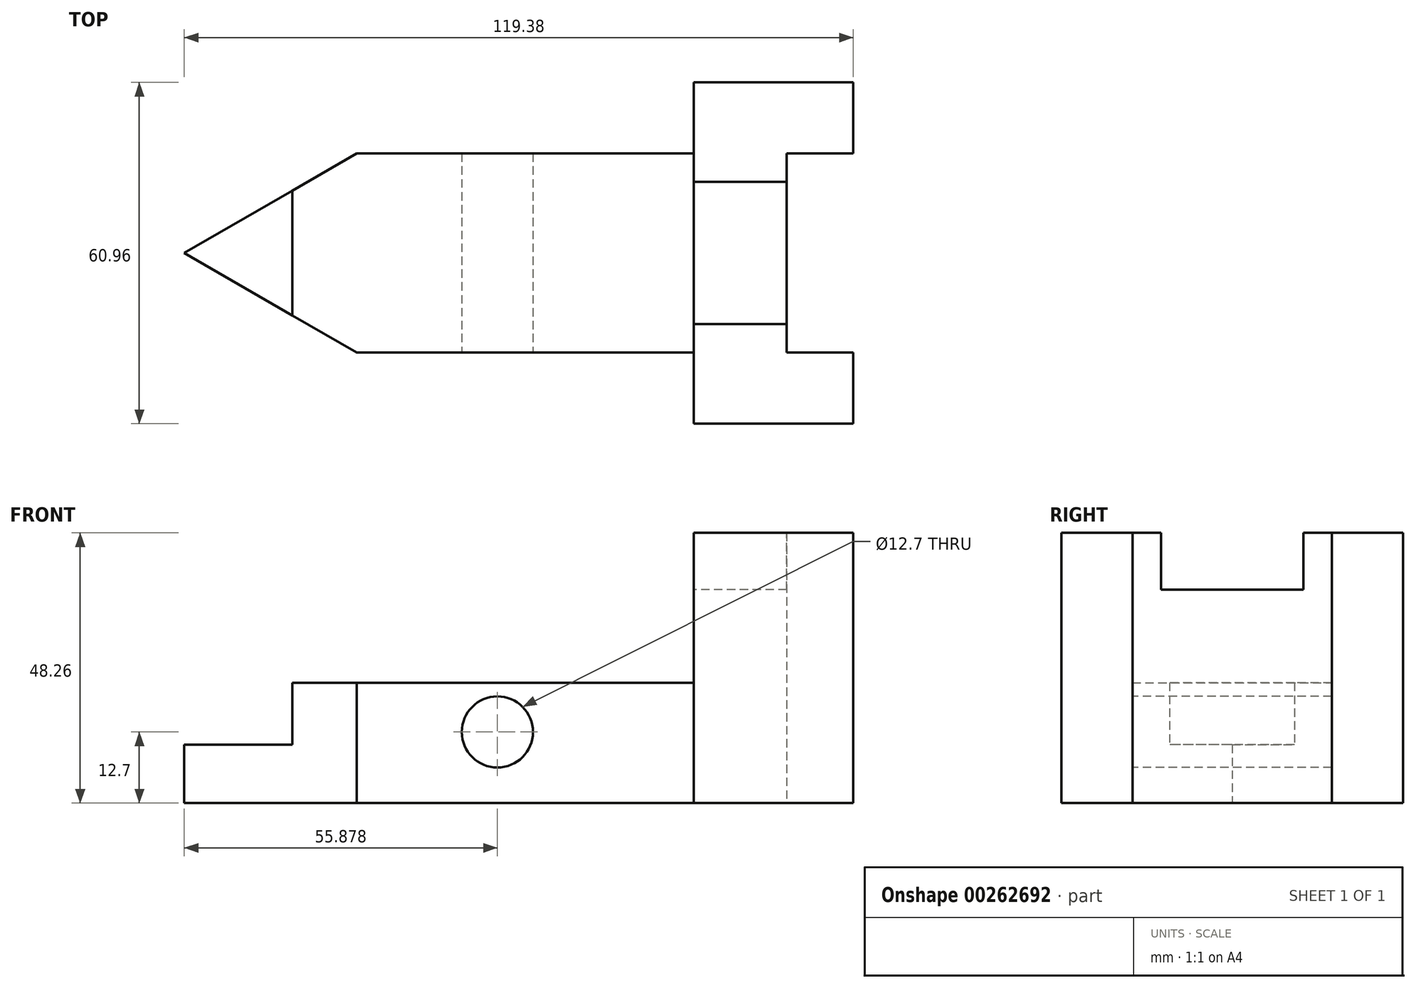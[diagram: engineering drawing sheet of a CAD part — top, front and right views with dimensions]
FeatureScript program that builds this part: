
annotation { "Feature Type Name" : "Feature", "Feature Type Description" : "" }
export const myFeature = defineFeature(function(context is Context, id is Id, definition is map)
    precondition{}
    {
        {
            var Q0;
            Q0=qCreatedBy(makeId("Top.planeOp"),FACE);
            var sketch = newSketch(context, id + "F0", { "sketchPlane" : qUnion([Q0])});
            skLineSegment(sketch, "E0.bottom", {"start": v(59.83, 28.5) * mm, "end": v(31.38, 28.5) * mm});
            skLineSegment(sketch, "E0.top", {"start": v(59.83, -32.46) * mm, "end": v(31.38, -32.46) * mm});
            skLineSegment(sketch, "E0.left", {"start": v(59.83, 28.5) * mm, "end": v(59.83, -32.46) * mm});
            skLineSegment(sketch, "E1", {"start": v(31.38, 28.5) * mm, "end": v(31.38, 15.8) * mm});
            skLineSegment(sketch, "E2.bottom", {"start": v(31.38, 15.8) * mm, "end": v(-28.76, 15.8) * mm});
            skLineSegment(sketch, "E2.top", {"start": v(31.38, -19.76) * mm, "end": v(-28.76, -19.76) * mm});
            skLineSegment(sketch, "E3", {"start": v(-59.55, -1.98) * mm, "end": v(-28.76, 15.8) * mm});
            skLineSegment(sketch, "E4", {"start": v(-59.55, -1.98) * mm, "end": v(-28.76, -19.76) * mm});
            skLineSegment(sketch, "E5.trimOffspring", {"start": v(31.38, -19.76) * mm, "end": v(31.38, -32.46) * mm});
            skSolve(sketch);
        }
        {
            var Q0;
            Q0 = qSketchRegion(id + "F0", true);
            extrude(context, id + "F1", {"entities" : qUnion([Q0]), "depth" : 48.26 * mm});
        }
        {
            var Q0;
            Q0=qCreatedBy(makeId("Front.planeOp"),FACE);
            var sketch = newSketch(context, id + "F2", { "sketchPlane" : qUnion([Q0])});
            skCircle(sketch, "E6", {"center": v(-3.67, 12.7) * mm, "radius": 6.35 * mm});
            skSolve(sketch);
        }
        {
            var Q0;
            Q0 = qSketchRegion(id + "F2", true);
            extrude(context, id + "F3", {"entities" : qUnion([Q0]), "operationType" : NewBodyOperationType.REMOVE, "endBound" : BoundingType.SYMMETRIC, "oppositeDirection" : true, "depth" : 40.13 * mm});
        }
        {
            var Q0;
            Q0=qCreatedBy(makeId("Front.planeOp"),FACE);
            var sketch = newSketch(context, id + "F4", { "sketchPlane" : qUnion([Q0])});
            skLineSegment(sketch, "E7.bottom", {"start": v(31.38, 48.3) * mm, "end": v(-59.55, 48.3) * mm});
            skLineSegment(sketch, "E7.top", {"start": v(31.38, 21.5) * mm, "end": v(-59.55, 21.5) * mm});
            skLineSegment(sketch, "E7.left", {"start": v(31.38, 48.3) * mm, "end": v(31.38, 21.5) * mm});
            skLineSegment(sketch, "E7.right", {"start": v(-59.55, 48.3) * mm, "end": v(-59.55, 21.5) * mm});
            skSolve(sketch);
        }
        {
            var Q0;
            Q0 = qSketchRegion(id + "F4", true);
            extrude(context, id + "F5", {"entities" : qUnion([Q0]), "operationType" : NewBodyOperationType.REMOVE, "endBound" : BoundingType.SYMMETRIC, "depth" : 127 * mm});
        }
        {
            var Q0;
            Q0=qCreatedBy(makeId("Top.planeOp"),FACE);
            var sketch = newSketch(context, id + "F6", { "sketchPlane" : qUnion([Q0])});
            skLineSegment(sketch, "E8.bottom", {"start": v(60.11, 15.8) * mm, "end": v(47.97, 15.8) * mm});
            skLineSegment(sketch, "E8.top", {"start": v(60.11, -19.76) * mm, "end": v(47.97, -19.76) * mm});
            skLineSegment(sketch, "E8.left", {"start": v(60.11, 15.8) * mm, "end": v(60.11, -19.76) * mm});
            skLineSegment(sketch, "E8.right", {"start": v(47.97, 15.8) * mm, "end": v(47.97, -19.76) * mm});
            skSolve(sketch);
        }
        {
            var Q0;
            Q0 = qSketchRegion(id + "F6", true);
            extrude(context, id + "F7", {"entities" : qUnion([Q0]), "operationType" : NewBodyOperationType.REMOVE, "depth" : 70.87 * mm});
        }
        {
            var Q0;
            Q0=makeQuery(id+"F1.opExtrude","CAP_FACE",FACE,{"disambiguationData":[OSD([sQuery(id+"F0.wireOp",EDGE,"E0.bottom"),sQuery(id+"F0.wireOp",EDGE,"E0.top"),sQuery(id+"F0.wireOp",EDGE,"E0.left"),sQuery(id+"F0.wireOp",EDGE,"E1"),sQuery(id+"F0.wireOp",EDGE,"E2.bottom"),sQuery(id+"F0.wireOp",EDGE,"E2.top"),sQuery(id+"F0.wireOp",EDGE,"E3"),sQuery(id+"F0.wireOp",EDGE,"E4"),sQuery(id+"F0.wireOp",EDGE,"E5.trimOffspring")])],"isStart":false});
            var sketch = newSketch(context, id + "F8", { "sketchPlane" : qUnion([Q0])});
            skLineSegment(sketch, "E9.bottom", {"start": v(56.8, 10.72) * mm, "end": v(21.02, 10.72) * mm});
            skLineSegment(sketch, "E9.top", {"start": v(56.8, -14.68) * mm, "end": v(21.02, -14.68) * mm});
            skLineSegment(sketch, "E9.left", {"start": v(56.8, 10.72) * mm, "end": v(56.8, -14.68) * mm});
            skLineSegment(sketch, "E9.right", {"start": v(21.02, 10.72) * mm, "end": v(21.02, -14.68) * mm});
            skSolve(sketch);
        }
        {
            var Q0;
            Q0 = qSketchRegion(id + "F8", true);
            extrude(context, id + "F9", {"entities" : qUnion([Q0]), "operationType" : NewBodyOperationType.REMOVE, "oppositeDirection" : true, "depth" : 10.16 * mm});
        }
        {
            var Q0;
            Q0=qCreatedBy(makeId("Top.planeOp"),FACE);
            var sketch = newSketch(context, id + "F10", { "sketchPlane" : qUnion([Q0])});
            skLineSegment(sketch, "E10.bottom", {"start": v(-40.25, 20.23) * mm, "end": v(-59.55, 20.23) * mm});
            skLineSegment(sketch, "E10.top", {"start": v(-40.25, -27.52) * mm, "end": v(-59.55, -27.52) * mm});
            skLineSegment(sketch, "E10.left", {"start": v(-40.25, 20.23) * mm, "end": v(-40.25, -27.52) * mm});
            skLineSegment(sketch, "E10.right", {"start": v(-59.55, 20.23) * mm, "end": v(-59.55, -27.52) * mm});
            skSolve(sketch);
        }
        {
            var Q0;
            Q0 = qSketchRegion(id + "F10", true);
            extrude(context, id + "F11", {"entities" : qUnion([Q0]), "operationType" : NewBodyOperationType.REMOVE, "depth" : 21.59 * mm, "hasSecondDirection" : true, "secondDirectionOppositeDirection" : false, "secondDirectionDepth" : 10.4 * mm});
        }
    });
